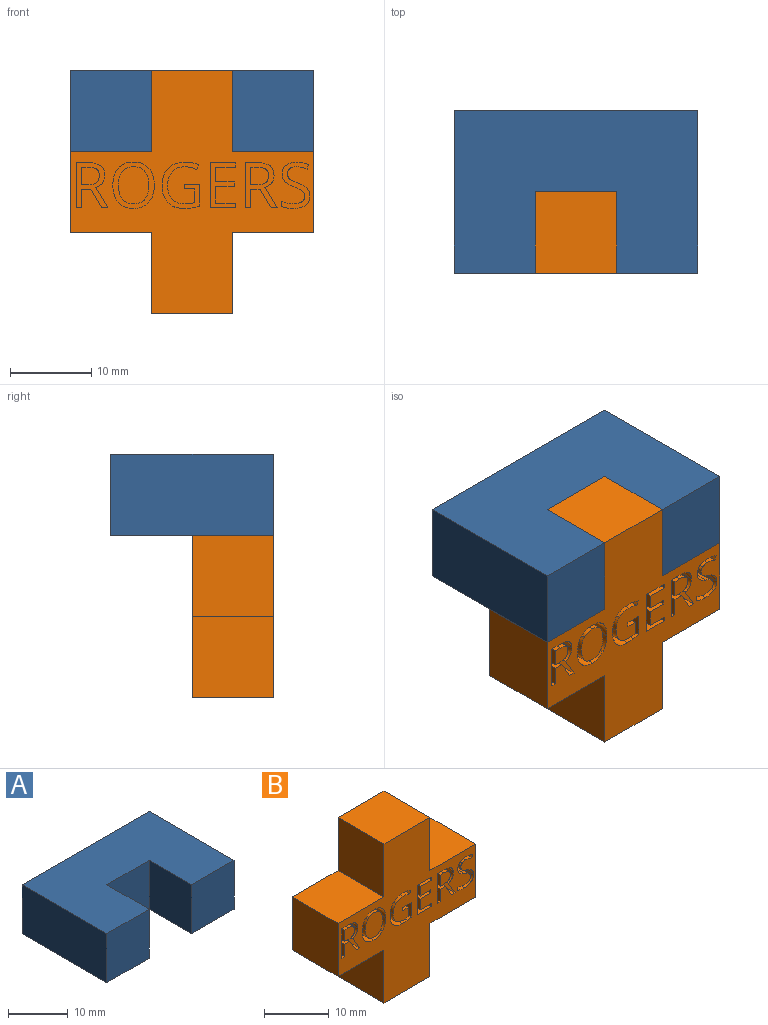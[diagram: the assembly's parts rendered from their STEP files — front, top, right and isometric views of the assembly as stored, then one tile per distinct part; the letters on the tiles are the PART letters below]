
ASSEMBLY  parts=2 mates=1
PART A: 10 faces, bbox 30x20x10 mm
  f0: plane 10x10mm, normal (0,-1,0), area 100mm2, adj f1,f7,f8,f9
  f1: plane 10x10mm, normal (1,0,0), area 100mm2, adj f0,f2,f8,f9
  f2: plane 10x10mm, normal (0,-1,0), area 100mm2, adj f1,f3,f8,f9
  f3: plane 10x10mm, normal (-1,0,0), area 100mm2, adj f2,f4,f8,f9
  f4: plane 10x10mm, normal (0,-1,0), area 100mm2, adj f3,f5,f8,f9
  f5: plane 20x10mm, normal (1,0,0), area 200mm2, adj f4,f6,f8,f9
  f6: plane 30x10mm, normal (0,1,0), area 300mm2, adj f5,f7,f8,f9
  f7: plane 20x10mm, normal (-1,0,0), area 200mm2, adj f0,f6,f8,f9
  f8: plane 30x20mm, normal (0,0,1), area 500mm2, adj f0,f1,f2,f3,f4,f5,f6,f7
  f9: plane 30x20mm, normal (0,0,-1), area 500mm2, adj f0,f1,f2,f3,f4,f5,f6,f7
PART B: 132 faces, bbox 30x10x30 mm
  f0: plane 30x30mm, normal (0,-1,0), area 425.2mm2, adj f1,f2,f3,f4,f5,f6,f7,f8
  f1: plane 10x10mm, normal (0,0,1), area 100mm2, adj f0,f2,f12,f13
  f2: plane 10x10mm, normal (-1,0,0), area 100mm2, adj f0,f1,f3,f13
  f3: plane 10x10mm, normal (0,0,1), area 100mm2, adj f0,f2,f4,f13
  f4: plane 10x10mm, normal (-1,0,0), area 100mm2, adj f0,f3,f5,f13
  f5: plane 10x10mm, normal (0,0,-1), area 100mm2, adj f0,f4,f6,f13
  f6: plane 10x10mm, normal (-1,0,0), area 100mm2, adj f0,f5,f7,f13
  f7: plane 10x10mm, normal (0,0,-1), area 100mm2, adj f0,f6,f8,f13
  f8: plane 10x10mm, normal (1,0,0), area 100mm2, adj f0,f7,f9,f13
  f9: plane 10x10mm, normal (0,0,-1), area 100mm2, adj f0,f8,f10,f13
  f10: plane 10x10mm, normal (1,0,0), area 100mm2, adj f0,f9,f11,f13
  f11: plane 10x10mm, normal (0,0,1), area 100mm2, adj f0,f10,f12,f13
  f12: plane 10x10mm, normal (1,0,0), area 100mm2, adj f0,f1,f11,f13
  f13: plane 30x30mm, normal (0,1,0), area 500mm2, adj f1,f2,f3,f4,f5,f6,f7,f8
  f14: plane 2.5x1.88mm, normal (0,0,-1), area 4.7mm2, adj f0,f15,f33,f34
  f15: plane 2.5x0.58mm, normal (1,0,0), area 1.4mm2, adj f0,f14,f16,f34
  f16: plane 2.5x1.24mm, normal (0,0,1), area 3.1mm2, adj f0,f15,f17,f34
  f17: plane 2.5x1.71mm, normal (1,0,0), area 4.3mm2, adj f0,f16,f18,f34
  f18: extruded ~2.5x1.13mm, area 2.8mm2, adj f0,f17,f19,f34
  f19: extruded ~2.5x1.61mm, area 4.4mm2, adj f0,f18,f20,f34
  f20: extruded ~2.5x1.7mm, area 4.6mm2, adj f0,f19,f21,f34
  f21: extruded ~2.5x1.67mm, area 4.5mm2, adj f0,f20,f22,f34
  f22: extruded ~2.5x1.58mm, area 4.4mm2, adj f0,f21,f23,f34
  f23: extruded ~2.5x1.44mm, area 3.7mm2, adj f0,f22,f24,f34
  f24: plane 2.5x0.57mm, normal (-0.92,0,0.4), area 1.6mm2, adj f0,f23,f25,f34
  f25: extruded ~2.5x1.65mm, area 4.2mm2, adj f0,f24,f26,f34
  f26: extruded ~2.5x1.53mm, area 3.9mm2, adj f0,f25,f27,f34
  f27: extruded ~2.5x1mm, area 3.6mm2, adj f0,f26,f28,f34
  f28: extruded ~2.5x1.52mm, area 3.9mm2, adj f0,f27,f29,f34
  f29: extruded ~2.5x2.1mm, area 5.7mm2, adj f0,f28,f30,f34
  f30: extruded ~2.5x1.96mm, area 5.4mm2, adj f0,f29,f31,f34
  f31: extruded ~2.5x1.05mm, area 2.6mm2, adj f0,f30,f32,f34
  f32: extruded ~2.5x0.9mm, area 2.3mm2, adj f0,f31,f33,f34
  f33: plane 2.7x2.5mm, normal (-1,0,0), area 6.7mm2, adj f0,f14,f32,f34
  f34: plane 5.7x4.61mm, normal (0,-1,0), area 9.3mm2, adj f14,f15,f16,f17,f18,f19,f20,f21
  f35: plane 2.5x0.88mm, normal (0,0,-1), area 2.2mm2, adj f36,f52,f53,f129
  f36: plane 2.5x2.12mm, normal (-1,0,0), area 5.3mm2, adj f35,f37,f53,f129
  f37: plane 2.5x0.84mm, normal (0,0,1), area 2.1mm2, adj f36,f38,f53,f129
  f38: extruded ~2.5x1.04mm, area 2.7mm2, adj f37,f39,f53,f129
  f39: extruded ~2.5x0.79mm, area 2.2mm2, adj f38,f40,f53,f129
  f40: extruded ~2.5x0.81mm, area 2.3mm2, adj f39,f52,f53,f129
  f41: plane 2.5x2.3mm, normal (-1,0,0), area 5.8mm2, adj f0,f42,f51,f53
  f42: plane 2.5x1.16mm, normal (0,0,1), area 2.9mm2, adj f0,f41,f43,f53
  f43: plane 2.5x2.3mm, normal (0.86,0,0.5), area 6.7mm2, adj f0,f42,f44,f53
  f44: plane 2.5x0.76mm, normal (0,0,1), area 1.9mm2, adj f0,f43,f45,f53
  f45: plane 2.5x2.49mm, normal (-0.86,0,-0.52), area 7.3mm2, adj f0,f44,f46,f53
  f46: extruded ~2.5x1.49mm, area 5mm2, adj f0,f45,f47,f53
  f47: extruded ~2.5x1.18mm, area 3.3mm2, adj f0,f46,f48,f53
  f48: extruded ~2.5x1.51mm, area 4mm2, adj f0,f47,f49,f53
  f49: plane 2.5x1.52mm, normal (0,0,-1), area 3.8mm2, adj f0,f48,f50,f53
  f50: plane 5.54x2.5mm, normal (1,0,0), area 13.9mm2, adj f0,f49,f51,f53
  f51: plane 2.5x0.64mm, normal (0,0,1), area 1.6mm2, adj f0,f41,f50,f53
  f52: extruded ~2.5x1mm, area 2.6mm2, adj f35,f40,f53,f129
  f53: plane 5.54x3.9mm, normal (0,-1,0), area 9.2mm2, adj f35,f36,f37,f38,f39,f40,f41,f42
  f54: extruded ~2.5x1.71mm, area 4.5mm2, adj f55,f69,f70,f130
  f55: extruded ~2.5x1.69mm, area 4.5mm2, adj f54,f56,f70,f130
  f56: extruded ~2.5x1.4mm, area 3.9mm2, adj f55,f57,f70,f130
  f57: extruded ~2.5x1.39mm, area 3.9mm2, adj f56,f58,f70,f130
  f58: extruded ~2.5x1.7mm, area 4.5mm2, adj f57,f59,f70,f130
  f59: extruded ~2.5x1.71mm, area 4.5mm2, adj f58,f60,f70,f130
  f60: extruded ~2.5x1.39mm, area 3.9mm2, adj f59,f69,f70,f130
  f61: extruded ~2.5x2.09mm, area 5.6mm2, adj f0,f62,f68,f70
  f62: extruded ~2.5x2.09mm, area 5.6mm2, adj f0,f61,f63,f70
  f63: extruded ~2.5x1.87mm, area 5.2mm2, adj f0,f62,f64,f70
  f64: extruded ~2.5x1.89mm, area 5.3mm2, adj f0,f63,f65,f70
  f65: extruded ~2.5x2.1mm, area 5.6mm2, adj f0,f64,f66,f70
  f66: extruded ~2.5x2.11mm, area 5.7mm2, adj f0,f65,f67,f70
  f67: extruded ~2.5x1.89mm, area 5.2mm2, adj f0,f66,f68,f70
  f68: extruded ~2.5x1.87mm, area 5.2mm2, adj f0,f61,f67,f70
  f69: extruded ~2.5x1.39mm, area 3.9mm2, adj f54,f60,f70,f130
  f70: plane 5.71x5.1mm, normal (0,-1,0), area 9.7mm2, adj f54,f55,f56,f57,f58,f59,f60,f61
  f71: plane 2.5x0.88mm, normal (0,0,-1), area 2.2mm2, adj f72,f88,f89,f131
  f72: plane 2.5x2.12mm, normal (-1,0,0), area 5.3mm2, adj f71,f73,f89,f131
  f73: plane 2.5x0.84mm, normal (0,0,1), area 2.1mm2, adj f72,f74,f89,f131
  f74: extruded ~2.5x1.04mm, area 2.7mm2, adj f73,f75,f89,f131
  f75: extruded ~2.5x0.79mm, area 2.2mm2, adj f74,f76,f89,f131
  f76: extruded ~2.5x0.81mm, area 2.3mm2, adj f75,f88,f89,f131
  f77: plane 2.5x2.3mm, normal (-1,0,0), area 5.8mm2, adj f0,f78,f87,f89
  f78: plane 2.5x1.16mm, normal (0,0,1), area 2.9mm2, adj f0,f77,f79,f89
  f79: plane 2.5x2.3mm, normal (0.86,0,0.5), area 6.7mm2, adj f0,f78,f80,f89
  f80: plane 2.5x0.76mm, normal (0,0,1), area 1.9mm2, adj f0,f79,f81,f89
  f81: plane 2.5x2.49mm, normal (-0.86,0,-0.52), area 7.3mm2, adj f0,f80,f82,f89
  f82: extruded ~2.5x1.49mm, area 5mm2, adj f0,f81,f83,f89
  f83: extruded ~2.5x1.18mm, area 3.3mm2, adj f0,f82,f84,f89
  f84: extruded ~2.5x1.51mm, area 4mm2, adj f0,f83,f85,f89
  f85: plane 2.5x1.52mm, normal (0,0,-1), area 3.8mm2, adj f0,f84,f86,f89
  f86: plane 5.54x2.5mm, normal (1,0,0), area 13.9mm2, adj f0,f85,f87,f89
  f87: plane 2.5x0.64mm, normal (0,0,1), area 1.6mm2, adj f0,f77,f86,f89
  f88: extruded ~2.5x1mm, area 2.6mm2, adj f71,f76,f89,f131
  f89: plane 5.54x3.9mm, normal (0,-1,0), area 9.2mm2, adj f71,f72,f73,f74,f75,f76,f77,f78
  f90: extruded ~2.5x1.14mm, area 3.3mm2, adj f0,f91,f114,f115
  f91: extruded ~2.5x0.92mm, area 2.5mm2, adj f0,f90,f92,f115
  f92: extruded ~2.5x1.2mm, area 3.5mm2, adj f0,f91,f93,f115
  f93: extruded ~2.5x0.77mm, area 2.1mm2, adj f0,f92,f94,f115
  f94: extruded ~2.5x0.36mm, area 1.2mm2, adj f0,f93,f95,f115
  f95: extruded ~2.5x0.47mm, area 1.2mm2, adj f0,f94,f96,f115
  f96: extruded ~2.5x0.61mm, area 1.8mm2, adj f0,f95,f97,f115
  f97: extruded ~2.5x0.8mm, area 2.1mm2, adj f0,f96,f98,f115
  f98: extruded ~2.5x1.33mm, area 3.4mm2, adj f0,f97,f99,f115
  f99: plane 2.5x0.56mm, normal (-0.94,0,0.34), area 1.5mm2, adj f0,f98,f100,f115
  f100: extruded ~2.5x1.52mm, area 3.9mm2, adj f0,f99,f101,f115
  f101: extruded ~2.5x1.27mm, area 3.4mm2, adj f0,f100,f102,f115
  f102: extruded ~2.5x1.02mm, area 2.9mm2, adj f0,f101,f103,f115
  f103: extruded ~2.5x0.99mm, area 2.7mm2, adj f0,f102,f104,f115
  f104: extruded ~2.5x1.1mm, area 3.2mm2, adj f0,f103,f105,f115
  f105: extruded ~2.5x0.82mm, area 2.2mm2, adj f0,f104,f106,f115
  f106: extruded ~2.5x0.39mm, area 1.3mm2, adj f0,f105,f107,f115
  f107: extruded ~2.5x0.47mm, area 1.2mm2, adj f0,f106,f108,f115
  f108: extruded ~2.5x0.68mm, area 2mm2, adj f0,f107,f109,f115
  f109: extruded ~2.5x0.97mm, area 2.5mm2, adj f0,f108,f110,f115
  f110: extruded ~2.5x0.8mm, area 2mm2, adj f0,f109,f111,f115
  f111: extruded ~2.5x0.74mm, area 1.9mm2, adj f0,f110,f112,f115
  f112: plane 2.5x0.62mm, normal (1,0,0), area 1.6mm2, adj f0,f111,f113,f115
  f113: extruded ~2.5x1.52mm, area 3.9mm2, adj f0,f112,f114,f115
  f114: extruded ~2.5x1.44mm, area 3.8mm2, adj f0,f90,f113,f115
  f115: plane 5.7x3.49mm, normal (0,-1,0), area 7.1mm2, adj f90,f91,f92,f93,f94,f95,f96,f97
  f116: plane 3.09x2.5mm, normal (0,0,1), area 7.7mm2, adj f0,f117,f127,f128
  f117: plane 2.5x0.58mm, normal (-1,0,0), area 1.4mm2, adj f0,f116,f118,f128
  f118: plane 2.5x2.45mm, normal (0,0,-1), area 6.1mm2, adj f0,f117,f119,f128
  f119: plane 2.5x2.04mm, normal (-1,0,0), area 5.1mm2, adj f0,f118,f120,f128
  f120: plane 2.5x2.3mm, normal (0,0,1), area 5.7mm2, adj f0,f119,f121,f128
  f121: plane 2.5x0.57mm, normal (-1,0,0), area 1.4mm2, adj f0,f120,f122,f128
  f122: plane 2.5x2.3mm, normal (0,0,-1), area 5.7mm2, adj f0,f121,f123,f128
  f123: plane 2.5x1.79mm, normal (-1,0,0), area 4.5mm2, adj f0,f122,f124,f128
  f124: plane 2.5x2.45mm, normal (0,0,1), area 6.1mm2, adj f0,f123,f125,f128
  f125: plane 2.5x0.57mm, normal (-1,0,0), area 1.4mm2, adj f0,f124,f126,f128
  f126: plane 3.09x2.5mm, normal (0,0,-1), area 7.7mm2, adj f0,f125,f127,f128
  f127: plane 5.54x2.5mm, normal (1,0,0), area 13.9mm2, adj f0,f116,f126,f128
  f128: plane 5.54x3.09mm, normal (0,-1,0), area 7.7mm2, adj f116,f117,f118,f119,f120,f121,f122,f123
  f129: plane 2.2x2.12mm, normal (0,-1,0), area 4.2mm2, adj f35,f36,f37,f38,f39,f40,f52
  f130: plane 4.56x3.73mm, normal (0,-1,0), area 14.1mm2, adj f54,f55,f56,f57,f58,f59,f60,f69
  f131: plane 2.2x2.12mm, normal (0,-1,0), area 4.2mm2, adj f71,f72,f73,f74,f75,f76,f88
PLACE A t=(-0.7,7.52,23.49)mm
PLACE B t=(-1.52,5.38,-6.08)mm
MATE fastened A.f7 <-> B.f4  axis (-1,0,0) through (-38.42,-4.62,23.49)mm
